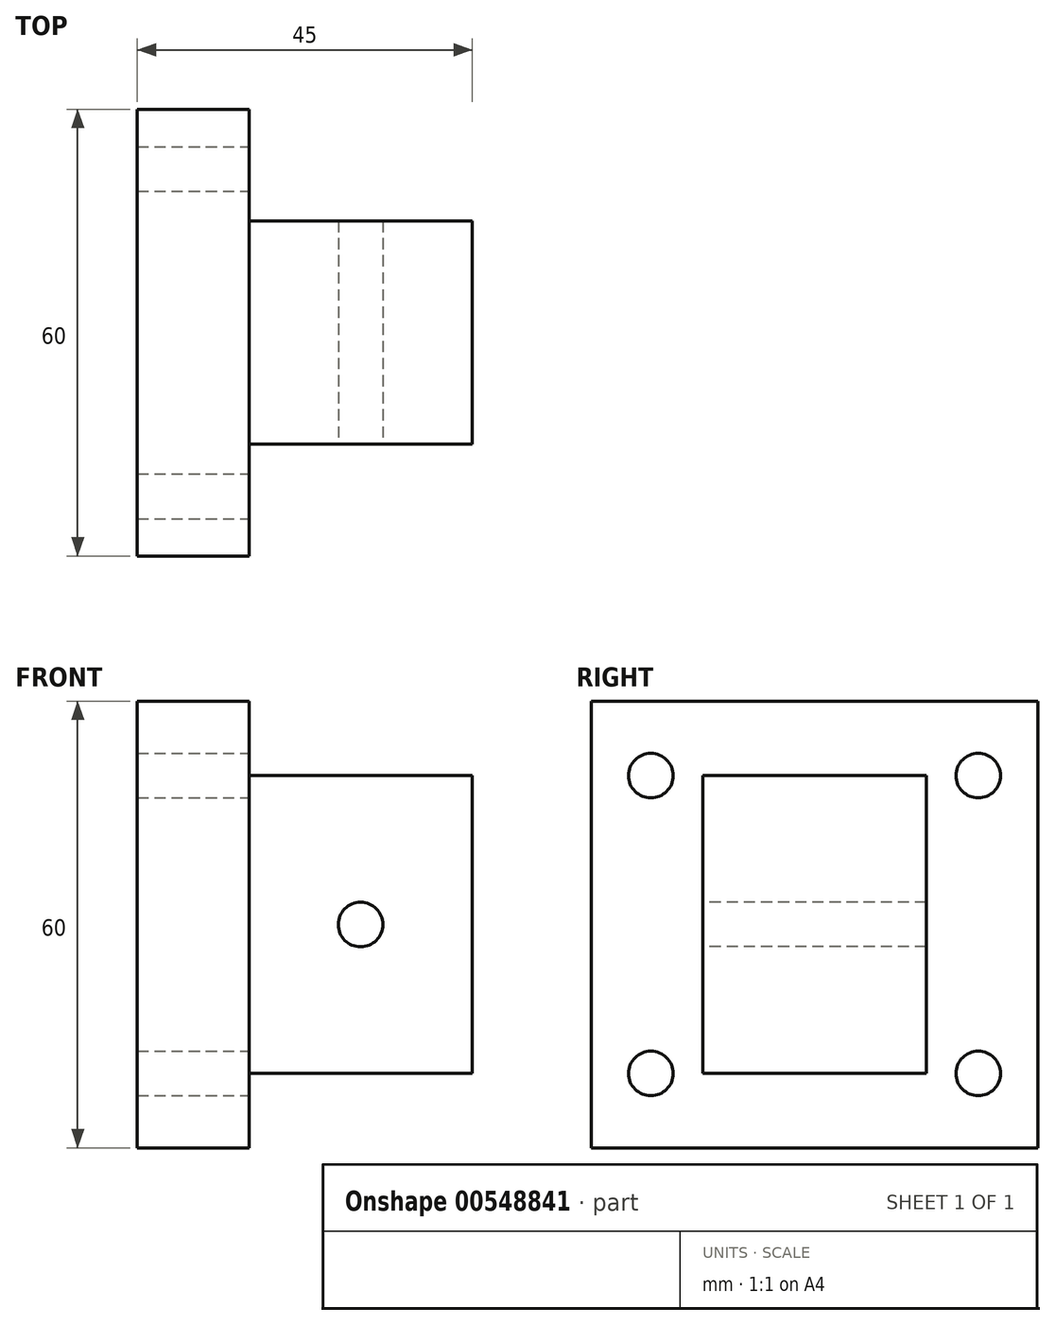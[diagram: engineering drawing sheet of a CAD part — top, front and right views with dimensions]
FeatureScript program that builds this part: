
annotation { "Feature Type Name" : "Feature", "Feature Type Description" : "" }
export const myFeature = defineFeature(function(context is Context, id is Id, definition is map)
    precondition{}
    {
        {
            var Q0;
            Q0=qCreatedBy(makeId("Right.planeOp"),FACE);
            var sketch = newSketch(context, id + "F0", { "sketchPlane" : qUnion([Q0])});
            skLineSegment(sketch, "E0.bottom", {"start": v(-30, 30) * mm, "end": v(30, 30) * mm});
            skLineSegment(sketch, "E0.top", {"start": v(-30, -30) * mm, "end": v(30, -30) * mm});
            skLineSegment(sketch, "E0.left", {"start": v(-30, 30) * mm, "end": v(-30, -30) * mm});
            skLineSegment(sketch, "E0.right", {"start": v(30, 30) * mm, "end": v(30, -30) * mm});
            skCircle(sketch, "E1", {"center": v(-22, 20) * mm, "radius": 3 * mm});
            skCircle(sketch, "E2", {"center": v(-22, -20) * mm, "radius": 3 * mm});
            skCircle(sketch, "E3", {"center": v(22, -20) * mm, "radius": 3 * mm});
            skCircle(sketch, "E4", {"center": v(22, 20) * mm, "radius": 3 * mm});
            skLineSegment(sketch, "E5.bottom", {"start": v(-15, 20) * mm, "end": v(15, 20) * mm});
            skLineSegment(sketch, "E5.top", {"start": v(-15, -20) * mm, "end": v(15, -20) * mm});
            skLineSegment(sketch, "E5.left", {"start": v(-15, 20) * mm, "end": v(-15, -20) * mm});
            skLineSegment(sketch, "E5.right", {"start": v(15, 20) * mm, "end": v(15, -20) * mm});
            skSolve(sketch);
        }
        {
            var Q0;
            Q0=makeQuery(id+"F0.imprint","IMPRINT",FACE,{"disambiguationData":[TD([[makeQuery(id+"F0.imprint","IMPRINT",EDGE,{"derivedFrom":sQuery(id+"F0.wireOp",EDGE,"E0.bottom")}),-1.0]])]});
            var Q1;
            Q1=makeQuery(id+"F0.imprint","IMPRINT",FACE,{"disambiguationData":[TD([[makeQuery(id+"F0.imprint","IMPRINT",EDGE,{"derivedFrom":sQuery(id+"F0.wireOp",EDGE,"u0jMUKhl-6n2V-fjkC-5YLW-VTPPdpPOOKdY")}),1.0]])]});
            var Q2;
            Q2=makeQuery(id+"F0.imprint","IMPRINT",FACE,{"disambiguationData":[TD([[makeQuery(id+"F0.imprint","IMPRINT",EDGE,{"derivedFrom":sQuery(id+"F0.wireOp",EDGE,"E5.bottom")}),-1.0]])]});
            extrude(context, id + "F1", {"entities" : qUnion([Q0, Q1, Q2]), "oppositeDirection" : true, "depth" : 15 * mm, "offsetDistance" : 25 * mm});
        }
        {
            var Q0;
            Q0=makeQuery(id+"F0.imprint","IMPRINT",FACE,{"disambiguationData":[TD([[makeQuery(id+"F0.imprint","IMPRINT",EDGE,{"derivedFrom":sQuery(id+"F0.wireOp",EDGE,"E5.bottom")}),-1.0]])]});
            extrude(context, id + "F2", {"entities" : qUnion([Q0]), "operationType" : NewBodyOperationType.ADD, "depth" : 30 * mm, "offsetDistance" : 25 * mm});
        }
        {
            var Q0;
            Q0=makeQuery(id+"F2.opExtrude","SWEPT_FACE",FACE,{"disambiguationData":[OSD([sQuery(id+"F0.wireOp",EDGE,"E5.left")])]});
            var sketch = newSketch(context, id + "F3", { "sketchPlane" : qUnion([Q0])});
            skCircle(sketch, "E6", {"center": v(15, 0) * mm, "radius": 3 * mm});
            skPoint(sketch, "E6.centerSnap0", {"position": v(15, 20) * mm});
            skSolve(sketch);
        }
        {
            var Q0;
            Q0=qSketchRegion(id+"F3",true);
            extrude(context, id + "F4", {"entities" : qUnion([Q0]), "operationType" : NewBodyOperationType.REMOVE, "endBound" : BoundingType.THROUGH_ALL, "oppositeDirection" : true, "depth" : 25 * mm, "offsetDistance" : 25 * mm});
        }
    });
